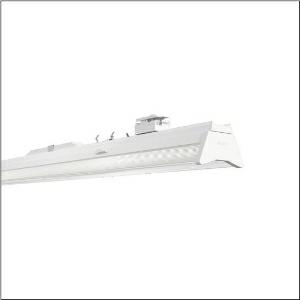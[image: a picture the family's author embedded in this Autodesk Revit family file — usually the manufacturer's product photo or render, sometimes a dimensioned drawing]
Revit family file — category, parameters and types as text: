
# Revit family: licross_11_performance_tw_51tm16tnt45x
name_source: partatom
category: Lighting Fixtures
units: mm (PartAtom-declared; Revit-internal decimal feet)

## family parameters
Cut with Voids When Loaded = No
Host = Face
Light Source = No
Part Type = Normal
Room Calculation Point = No
Round Connector Dimension = Use Diameter
Shared = No

## types (1)
- --- (1 x LED 2700 K ... 6500 K, 4700 lm, 28.9 W, 2700K)
    Apparent Load = 29 VA
    CIE Flux Codes = 63 87 95 78 100
    Color Rendering = 80
    Color Temperature = 2700K
    Default Elevation = 1800 mm
    Description = Licross 11 Performance TW, luminaire insert, of sheet steel, galvanised, coil coated, white, length: 1.500mm, width: 120mm, height: 123mm, LED rated luminous flux: 4.700lm, light colour: 8tw, SDCM (Standard Deviation of Colour Matching)MacAdam ≤ 2 SDCM (initial), control gear: DALI DT8, with plug, 5-pole, with phase selection, mains connection: 220..240V, AC, 50/60Hz, rated input power: 28.9W, internal wiring halogen-free, primary light control with lens, of plastic, primary optical cover: cover, of PMMA, light emission: direct/indirect distribution, primary light characteristic: symmetric, protection rating (complete): IP40, insulation class (complete): insulation class I (protective earthing), certification: CE, ENEC, VDE, UKCA, protection symbol: D if used in an environment without relevant dust loads with corresponding accessories, impact resistance: IK06, permissible ambient temperature for indoor applications: -25..+45°C, corresponds to IFS (International Featured Standards) requirements for safety and quality in the food industry, reducing of maximum allowable ambient temperature of 5°C with ceiling mounting, LABS conformity tested according to VDMA 24364:2018-05, The light source and the operating device comply with the requirements of the Ecodesign Regulation (EU) 2019/2020 and are replaceable in accordance with this regulation, packaging unit: 1 piece
    Height = 114 mm
    Lamp = 1 x LED 2700 K ... 6500 K
    Lamp Light Flux = 4700 lm
    Lamp Power = 28.9 W
    Lamp count = 1
    Length = 1500 mm
    Luminous efficacy = 163 lm/W
    Manufacturer = Siteco
    ModVariant = No
    Model = 51TM16TNT45X
    Mounting Place = Ceiling
    Mounting Type = Pendant
    Number of Poles = 1
    OnlyDefault = Yes
    Power Factor = 1
    Product Name = Licross 11 Performance TW
    Product group = luminaire insert | ceiling pendant
    ProductGroupID = 901
    Protection Class = Protection class I
    Protection Degree = IP 40
    RLX_Detail_Level = 1
    RLX_Emergency_Light_Flux = 0 lm
    RLX_Emergency_Type = 0
    RLX_Emergency_Type_DB = No
    RlxData = <blob elided: 30653 chars, md5=78888a3e>
    Socket = socket
    Standby Power = 0 W
    System Light Flux = 4700 lm
    System Power = 29 W
    Type Comments = individual setting: CCT=2700K
    Type Image = l_1256138.jpg
    URL = http://relux.com
    VarID = @adj_056359
    Voltage = 0 V
    Weight = 0.00 kg
    Width = 120 mm

## geometry (parser evidence)
native form markers: Blend x4, Sweep x13
no freeform markers — native parametric forms only
